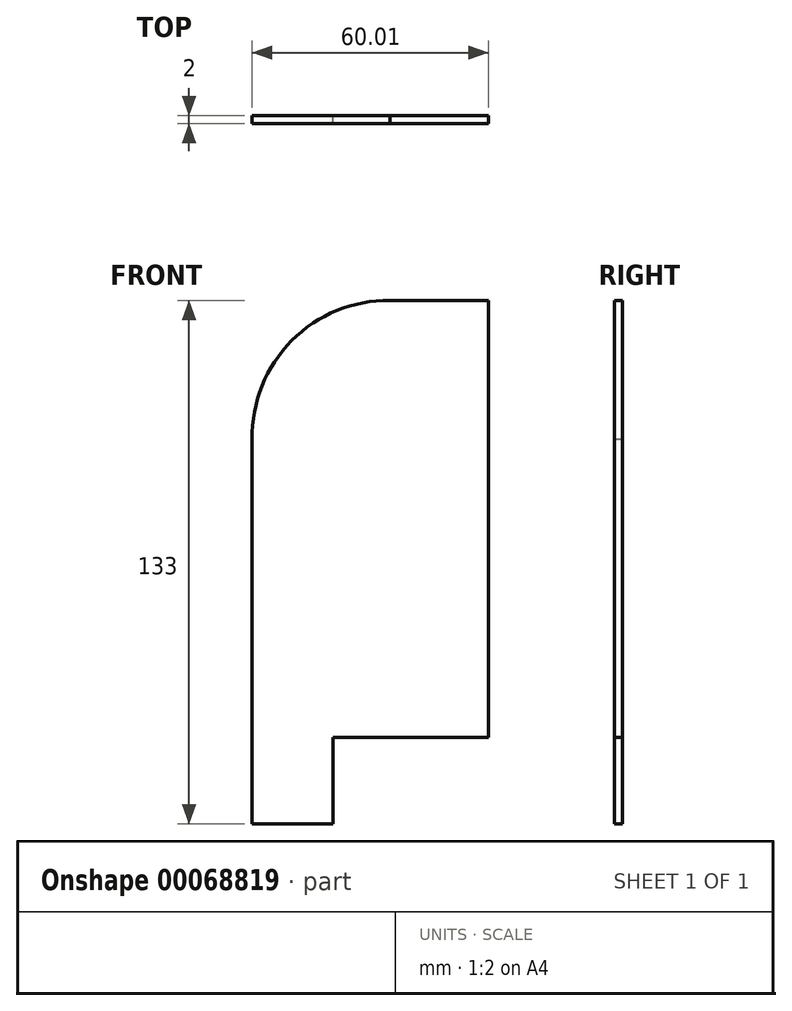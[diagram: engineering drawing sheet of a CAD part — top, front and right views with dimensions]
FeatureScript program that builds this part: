
annotation { "Feature Type Name" : "Feature", "Feature Type Description" : "" }
export const myFeature = defineFeature(function(context is Context, id is Id, definition is map)
    precondition{}
    {
        {
            var Q0;
            Q0=qCreatedBy(makeId("Front.planeOp"),FACE);
            var sketch = newSketch(context, id + "F0", { "sketchPlane" : qUnion([Q0])});
            skLineSegment(sketch, "E0", {"start": v(-430.79, -17.28) * mm, "end": v(-410.29, -17.28) * mm});
            skLineSegment(sketch, "E1", {"start": v(-410.29, -17.28) * mm, "end": v(-410.29, 4.72) * mm});
            skLineSegment(sketch, "E2", {"start": v(-410.29, 4.72) * mm, "end": v(-395.79, 4.72) * mm});
            skLineSegment(sketch, "E3", {"start": v(-395.79, 4.72) * mm, "end": v(-395.79, 115.72) * mm});
            skLineSegment(sketch, "E4", {"start": v(-430.79, 80.47) * mm, "end": v(-430.79, -17.28) * mm});
            skArc(sketch, "E5", {"start": v(-395.79, 115.72) * mm, "mid": v(-420.77, 105.52) * mm, "end": v(-430.79, 80.47) * mm});
            skLineSegment(sketch, "E6.bottom", {"start": v(-395.79, 4.72) * mm, "end": v(-370.79, 4.72) * mm});
            skLineSegment(sketch, "E6.top", {"start": v(-395.79, 115.72) * mm, "end": v(-370.79, 115.72) * mm});
            skLineSegment(sketch, "E6.right", {"start": v(-370.79, 4.72) * mm, "end": v(-370.79, 115.72) * mm});
            skSolve(sketch);
        }
        {
            var Q0;
            Q0 = qSketchRegion(id + "F0", true);
            extrude(context, id + "F1", {"entities" : qUnion([Q0]), "depth" : 2 * mm});
        }
    });
